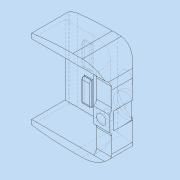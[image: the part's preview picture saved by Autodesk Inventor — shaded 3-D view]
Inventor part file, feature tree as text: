
AUTODESK INVENTOR PART (.ipt)
format: ipt  version: 2014 (Build 180170000, 170)  size: 303,616 bytes
history: native  units: in
note: dims shown in document units (in); Inventor stores cm internally (conversion verified against a paired STEP export)
features: fillet x10, extrude x8, sketch x8, chamfer x6, other x1, projected_geometry x1
ambient origin geometry x8: Origin, YZ Plane, XZ Plane, XY Plane, X Axis, Y Axis, Z Axis, Center Point
bodies: Solid1 (feature_tree)
feature tree (34):
  other  "batterybox_sketch.ipt"
  extrude  "Extrusion1"  Depth=0.3937in TaperAngle=0.0deg
  extrude  "Extrusion2"  Depth=0.1875in TaperAngle=0.0deg
  extrude  "Extrusion3"  Depth=2.0079in
  fillet  "Fillet1"  Radius=2.0079in
  extrude  "Extrusion4"  Depth=0.5in
  extrude  "Extrusion7"  Depth=0.5in
  extrude  "Extrusion8"  Depth=0.125in
  chamfer  "Chamfer5"  Distance=1.0in
  extrude  "Extrusion9"  Depth=0.5in
  chamfer  "Chamfer12"  Distance=2.7579in
  extrude  "Extrusion23"  Depth=0.5in TaperAngle=0.0deg
  chamfer  "Chamfer13"  Distance=0.6in
  chamfer  "Chamfer14"  Distance=0.5in
  fillet  "Fillet23"  Radius=1.5in
  chamfer  "Chamfer16"  Distance=1.0in
  fillet  "Fillet24"  Radius=1.0625in
  chamfer  "Chamfer17"  Distance=1.0in Angle=45.0deg
  fillet  "Fillet25"  Radius=0.5in
  fillet  "Fillet26"  Radius=0.5in
  fillet  "Fillet27"  Radius=0.1875in
  fillet  "Fillet28"  Radius=0.75in
  fillet  "Fillet29"  Radius=0.75in
  fillet  "Fillet30"  Radius=0.3125in
  fillet  "Fillet31"  Radius=0.1in
  sketch  "Sketch1"  dims[d0=0.3937in d1=4.0in d2=0.0in]
  sketch  "Sketch2"  dims[d4=1.25in d5=0.1875in d6=0.0in]
  sketch  "Sketch3"  dims[d7=4.5157in d8=2.0079in d9=2.0079in]
  sketch  "Sketch4"  dims[d10=0.5in d11=0.5in]
  sketch  "Sketch7"  dims[d12=1.5in d13=0.0in d14=0.5in]
  sketch  "Sketch8"  dims[d15=0.0312in d16=0.0312in d17=0.125in d18=1.0in d19=0.0in]
  sketch  "Sketch9"  dims[d41=0.201in d42=0.5in]
  sketch  "Sketch23"  dims[d43=5.5157in d44=2.7579in d45=0.5in d46=0.0in d47=0.6in d48=0.5in d49=0.0in d50=1.5in d51=1.0in d52=0.0in d67=1.0625in d68=0.125in d69=45.0deg d167=1.0in d168=0.125in d169=45.0deg d170=0.5in d171=0.5in d172=0.1875in d173=0.0in d174=0.75in d175=0.125in d176=45.0deg d177=0.75in d178=0.125in d179=45.0deg d191=0.3125in d195=0.1in d196=0.125in d197=45.0deg d198=7.5in d199=0.1875in d200=0.125in d201=45.0deg d202=19.0625in d203=2.375in d204=2.375in d205=0.5in d206=0.5in d207=2.6875in d208=2.6875in]
  projected_geometry  "Projected Loop5"
